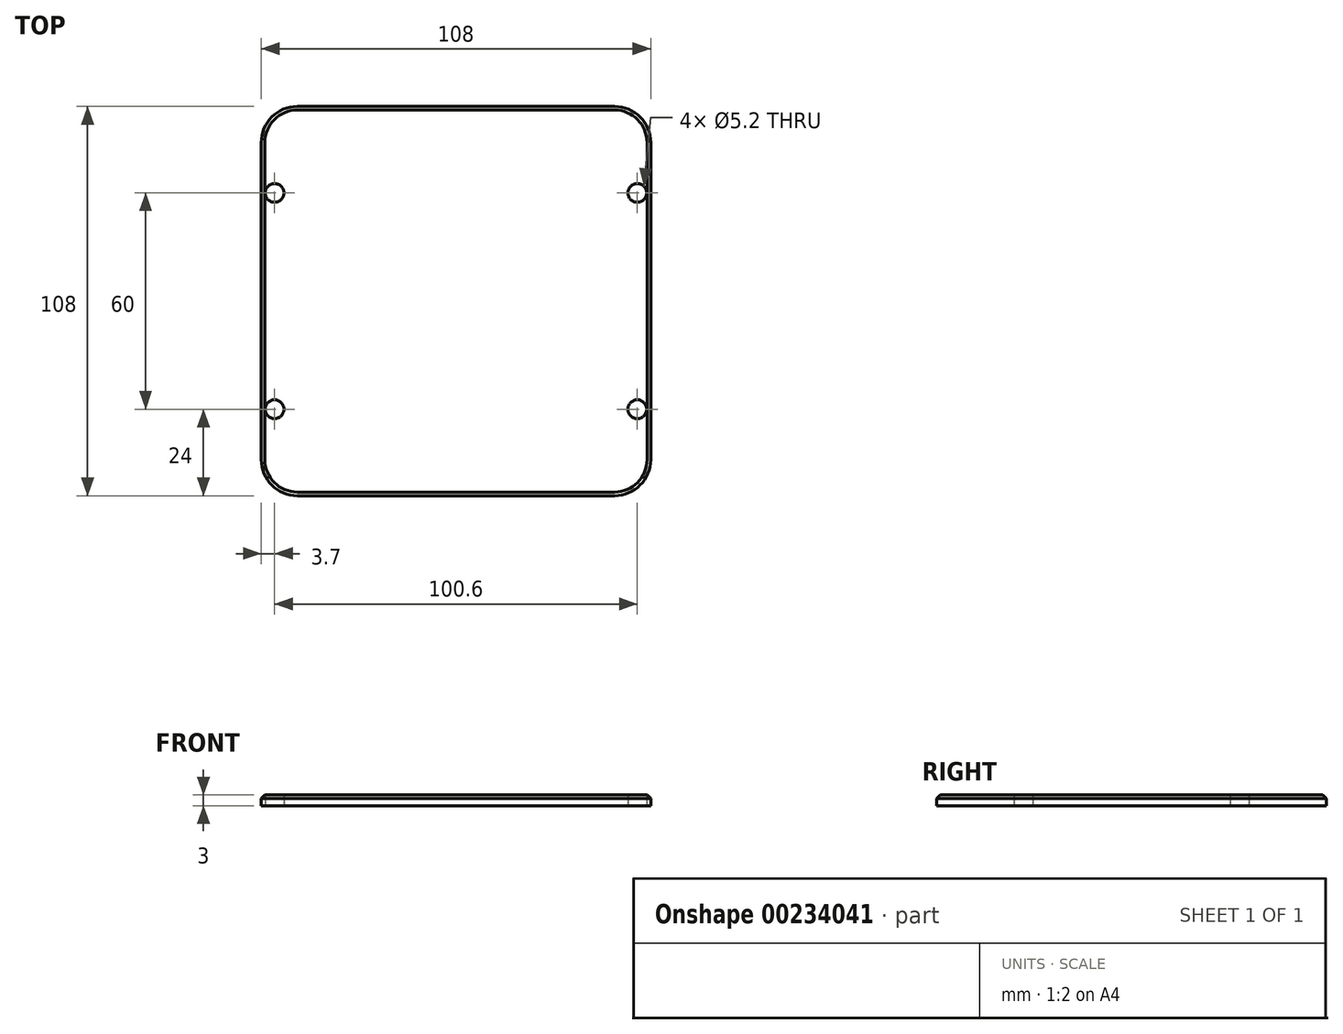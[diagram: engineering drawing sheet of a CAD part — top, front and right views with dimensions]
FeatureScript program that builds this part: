
annotation { "Feature Type Name" : "Feature", "Feature Type Description" : "" }
export const myFeature = defineFeature(function(context is Context, id is Id, definition is map)
    precondition{}
    {
        {
            var Q0;
            Q0=qCreatedBy(makeId("Top.planeOp"),FACE);
            var sketch = newSketch(context, id + "F0", { "sketchPlane" : qUnion([Q0])});
            skPoint(sketch, "E0.visualSharp", {"position": v(-60, 60) * mm});
            skPoint(sketch, "E1.visualSharp", {"position": v(-60, -60) * mm});
            skPoint(sketch, "E2.visualSharp", {"position": v(50, -60) * mm});
            skPoint(sketch, "E3.visualSharp", {"position": v(50, 60) * mm});
            skLineSegment(sketch, "E4.bottom", {"start": v(50.3, -30) * mm, "end": v(-50.3, -30) * mm, "construction": true});
            skLineSegment(sketch, "E4.top", {"start": v(50.3, 30) * mm, "end": v(-50.3, 30) * mm, "construction": true});
            skLineSegment(sketch, "E4.left", {"start": v(50.3, -30) * mm, "end": v(50.3, 30) * mm, "construction": true});
            skLineSegment(sketch, "E4.right", {"start": v(-50.3, -30) * mm, "end": v(-50.3, 30) * mm, "construction": true});
            skCircle(sketch, "E5", {"center": v(-50.3, 30) * mm, "radius": 2.6 * mm});
            skCircle(sketch, "E6", {"center": v(50.3, 30) * mm, "radius": 2.6 * mm});
            skCircle(sketch, "E7", {"center": v(-50.3, -30) * mm, "radius": 2.6 * mm});
            skCircle(sketch, "E8", {"center": v(50.3, -30) * mm, "radius": 2.6 * mm});
            skLineSegment(sketch, "E9.bottom", {"start": v(44, -54) * mm, "end": v(-44, -54) * mm});
            skLineSegment(sketch, "E9.top", {"start": v(44, 54) * mm, "end": v(-44, 54) * mm});
            skLineSegment(sketch, "E9.left", {"start": v(54, -44) * mm, "end": v(54, 44) * mm});
            skLineSegment(sketch, "E9.right", {"start": v(-54, -44) * mm, "end": v(-54, 44) * mm});
            skPoint(sketch, "E9.middle", {"position": v(0, 0) * mm});
            skPoint(sketch, "E10.visualSharp", {"position": v(-54, 54) * mm});
            skArc(sketch, "E10.filletArc", {"start": v(-44, 54) * mm, "mid": v(-51.07, 51.07) * mm, "end": v(-54, 44) * mm});
            skPoint(sketch, "E11.visualSharp", {"position": v(54, 54) * mm});
            skArc(sketch, "E11.filletArc", {"start": v(54, 44) * mm, "mid": v(51.07, 51.07) * mm, "end": v(44, 54) * mm});
            skPoint(sketch, "E12.visualSharp", {"position": v(54, -54) * mm});
            skArc(sketch, "E12.filletArc", {"start": v(44, -54) * mm, "mid": v(51.07, -51.07) * mm, "end": v(54, -44) * mm});
            skPoint(sketch, "E13.visualSharp", {"position": v(-54, -54) * mm});
            skArc(sketch, "E13.filletArc", {"start": v(-54, -44) * mm, "mid": v(-51.07, -51.07) * mm, "end": v(-44, -54) * mm});
            skSolve(sketch);
        }
        {
            var Q0;
            Q0=qSketchRegion(id+"F0",true);
            extrude(context, id + "F1", {"entities" : qUnion([Q0]), "depth" : 3 * mm});
        }
        {
            var Q0;
            Q0=makeQuery(id+"F1.opExtrude","CAP_EDGE",EDGE,{"disambiguationData":[OSD([sQuery(id+"F0.wireOp",EDGE,"E9.top")])],"isStart":false});
            chamfer(context, id + "F2", {"entities" : qUnion([Q0]), "width" : 1 * mm, "tangentPropagation" : true});
        }
    });
